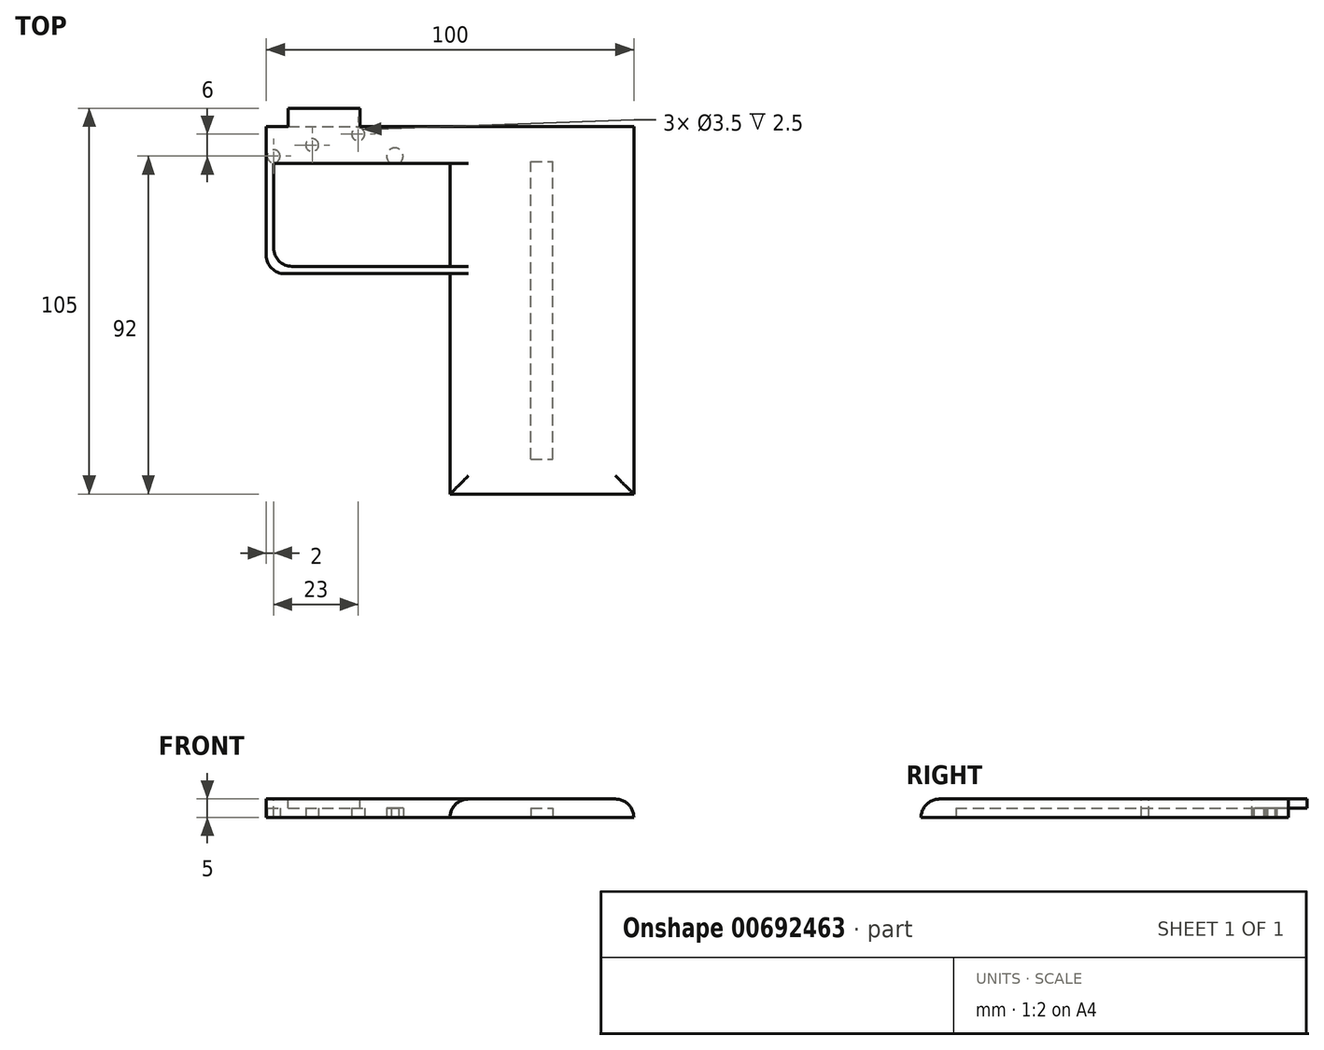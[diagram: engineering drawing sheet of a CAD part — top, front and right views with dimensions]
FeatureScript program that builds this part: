
annotation { "Feature Type Name" : "Feature", "Feature Type Description" : "" }
export const myFeature = defineFeature(function(context is Context, id is Id, definition is map)
    precondition{}
    {
        {
            var Q0;
            Q0=qCreatedBy(makeId("Top.planeOp"),FACE);
            var sketch = newSketch(context, id + "F0", { "sketchPlane" : qUnion([Q0])});
            skLineSegment(sketch, "E0.bottom", {"start": v(25, 50) * mm, "end": v(-25, 50) * mm});
            skLineSegment(sketch, "E0.top", {"start": v(25, -50) * mm, "end": v(-25, -50) * mm});
            skLineSegment(sketch, "E0.left", {"start": v(25, 50) * mm, "end": v(25, -50) * mm});
            skLineSegment(sketch, "E0.right", {"start": v(-25, 50) * mm, "end": v(-25, -50) * mm});
            skPoint(sketch, "E0.middle", {"position": v(0, 0) * mm});
            skLineSegment(sketch, "E1.bottom", {"start": v(-25, 50) * mm, "end": v(-75, 50) * mm});
            skLineSegment(sketch, "E1.top", {"start": v(-25, 10) * mm, "end": v(-75, 10) * mm});
            skLineSegment(sketch, "E1.left", {"start": v(-25, 50) * mm, "end": v(-25, 10) * mm});
            skLineSegment(sketch, "E1.right", {"start": v(-75, 50) * mm, "end": v(-75, 10) * mm});
            skLineSegment(sketch, "E2", {"start": v(-75, 50) * mm, "end": v(-73, 50) * mm});
            skLineSegment(sketch, "E3", {"start": v(-73, 50) * mm, "end": v(-73, 40) * mm});
            skLineSegment(sketch, "E4", {"start": v(-25, 10) * mm, "end": v(-25, 12) * mm});
            skLineSegment(sketch, "E5.bottom", {"start": v(-25, 12) * mm, "end": v(-73, 12) * mm});
            skLineSegment(sketch, "E5.top", {"start": v(-25, 40) * mm, "end": v(-73, 40) * mm});
            skLineSegment(sketch, "E5.left", {"start": v(-25, 12) * mm, "end": v(-25, 40) * mm});
            skLineSegment(sketch, "E5.right", {"start": v(-73, 12) * mm, "end": v(-73, 40) * mm});
            skSolve(sketch);
        }
        {
            var Q0;
            {var subQ0=sQuery(id+"F0.wireOp",EDGE,"E2");Q0=makeQuery(id+"F0.imprint","IMPRINT",FACE,{"disambiguationData":[TD([[makeQuery(id+"F0.imprint","IMPRINT",EDGE,{"derivedFrom":subQ0}),-1.0]])]});}
            var Q1;
            {var subQ2=sQuery(id+"F0.wireOp",EDGE,"E1.top");Q1=makeQuery(id+"F0.imprint","IMPRINT",FACE,{"disambiguationData":[TD([[makeQuery(id+"F0.imprint","IMPRINT",EDGE,{"derivedFrom":subQ2}),-1.0]])]});}
            var Q2;
            {var subQ1=sQuery(id+"F0.wireOp",EDGE,"E0.bottom");Q2=makeQuery(id+"F0.imprint","IMPRINT",FACE,{"disambiguationData":[TD([[makeQuery(id+"F0.imprint","IMPRINT",EDGE,{"derivedFrom":subQ1}),1.0]])]});}
            var Q3;
            {var subQ4=sQuery(id+"F0.wireOp",EDGE,"E1.bottom");Q3=makeQuery(id+"F0.imprint","IMPRINT",FACE,{"disambiguationData":[TD([[makeQuery(id+"F0.imprint","IMPRINT",EDGE,{"derivedFrom":subQ4}),1.0]])]});}
            extrude(context, id + "F1", {"entities" : qUnion([Q0, Q1, Q2, Q3]), "oppositeDirection" : true, "depth" : 5 * mm, "offsetDistance" : 25 * mm});
        }
        {
            var Q0;
            Q0=makeQuery(id+"F1.opExtrude","CAP_EDGE",EDGE,{"disambiguationData":[OSD([sQuery(id+"F0.wireOp",EDGE,"E0.right")])],"isStart":true});
            var Q1;
            Q1=makeQuery(id+"F1.opExtrude","CAP_EDGE",EDGE,{"disambiguationData":[OSD([sQuery(id+"F0.wireOp",EDGE,"E0.top")])],"isStart":true});
            var Q2;
            Q2=makeQuery(id+"F1.opExtrude","CAP_EDGE",EDGE,{"disambiguationData":[OSD([sQuery(id+"F0.wireOp",EDGE,"E0.left")])],"isStart":true});
            var Q3;
            Q3=makeQuery(id+"F1.opExtrude","CAP_EDGE",EDGE,{"disambiguationData":[OSD([sQuery(id+"F0.wireOp",EDGE,"E5.left")])],"isStart":true});
            fillet(context, id + "F2", {"entities" : qUnion([Q0, Q1, Q2, Q3]), "radius" : 5 * mm, "tangentPropagation" : true, "allowEdgeOverflow" : false});
        }
        {
            var Q0;
            Q0=makeQuery(id+"F1.opExtrude","SWEPT_EDGE",EDGE,{"disambiguationData":[OSD([sQuery(id+"F0.wireOp",EDGE,"E5.bottom"),sQuery(id+"F0.wireOp",EDGE,"E5.right")])]});
            var Q1;
            Q1=makeQuery(id+"F1.opExtrude","SWEPT_EDGE",EDGE,{"disambiguationData":[OSD([sQuery(id+"F0.wireOp",EDGE,"E1.top"),sQuery(id+"F0.wireOp",EDGE,"E1.right")])]});
            fillet(context, id + "F3", {"entities" : qUnion([Q0, Q1]), "radius" : 5 * mm, "tangentPropagation" : true, "allowEdgeOverflow" : false});
        }
        {
            var Q0;
            Q0=makeQuery(id+"F1.opExtrude","CAP_FACE",FACE,{"disambiguationData":[OSD([sQuery(id+"F0.wireOp",EDGE,"E0.bottom"),sQuery(id+"F0.wireOp",EDGE,"E0.top"),sQuery(id+"F0.wireOp",EDGE,"E0.left"),sQuery(id+"F0.wireOp",EDGE,"E0.right"),sQuery(id+"F0.wireOp",EDGE,"E1.bottom"),sQuery(id+"F0.wireOp",EDGE,"E1.top"),sQuery(id+"F0.wireOp",EDGE,"E1.right"),sQuery(id+"F0.wireOp",EDGE,"E2"),sQuery(id+"F0.wireOp",EDGE,"E5.bottom"),sQuery(id+"F0.wireOp",EDGE,"E5.top"),sQuery(id+"F0.wireOp",EDGE,"E5.left"),sQuery(id+"F0.wireOp",EDGE,"E5.right")])],"isStart":false});
            var sketch = newSketch(context, id + "F4", { "sketchPlane" : qUnion([Q0])});
            skLineSegment(sketch, "E6", {"start": v(-25, -40) * mm, "end": v(-40, -40) * mm, "construction": true});
            skLineSegment(sketch, "E7", {"start": v(-40, -40) * mm, "end": v(-40, -42) * mm, "construction": true});
            skCircle(sketch, "E8", {"center": v(-40, -42) * mm, "radius": 2.25 * mm});
            skLineSegment(sketch, "E9", {"start": v(-40, -40) * mm, "end": v(-62.5, -40) * mm, "construction": true});
            skLineSegment(sketch, "E10", {"start": v(-62.5, -40) * mm, "end": v(-62.5, -45) * mm, "construction": true});
            skCircle(sketch, "E11", {"center": v(-62.5, -45) * mm, "radius": 1.75 * mm});
            skLineSegment(sketch, "E12", {"start": v(-40, -42) * mm, "end": v(-40, -50) * mm, "construction": true});
            skLineSegment(sketch, "E13", {"start": v(-40, -50) * mm, "end": v(-50, -50) * mm, "construction": true});
            skLineSegment(sketch, "E14", {"start": v(-50, -50) * mm, "end": v(-50, -48) * mm, "construction": true});
            skCircle(sketch, "E15", {"center": v(-50, -48) * mm, "radius": 1.75 * mm});
            skLineSegment(sketch, "E16", {"start": v(-73, -40) * mm, "end": v(-73, -42) * mm});
            skCircle(sketch, "E17", {"center": v(-73, -42) * mm, "radius": 1.75 * mm});
            skLineSegment(sketch, "E18.bottom", {"start": v(-3, 40.5) * mm, "end": v(3, 40.5) * mm});
            skLineSegment(sketch, "E18.top", {"start": v(-3, -40.5) * mm, "end": v(3, -40.5) * mm});
            skLineSegment(sketch, "E18.left", {"start": v(-3, 40.5) * mm, "end": v(-3, -40.5) * mm});
            skLineSegment(sketch, "E18.right", {"start": v(3, 40.5) * mm, "end": v(3, -40.5) * mm});
            skPoint(sketch, "E18.middle", {"position": v(0, 0) * mm});
            skSolve(sketch);
        }
        {
            var Q0;
            Q0=makeQuery(id+"F4.imprint","IMPRINT",FACE,{"disambiguationData":[TD([[makeQuery(id+"F4.imprint","IMPRINT",EDGE,{"derivedFrom":sQuery(id+"F4.wireOp",EDGE,"E18.bottom")}),-1.0]])]});
            var Q1;
            {var subQ0=sQuery(id+"F4.wireOp",EDGE,"E8");var subQ1=makeQuery(id+"F1.opExtrude","CAP_EDGE",EDGE,{"disambiguationData":[OSD([sQuery(id+"F0.wireOp",EDGE,"E5.top")])],"isStart":false});var subQ2=makeQuery(id+"F4.imprint","INTERSECT",VERTEX,{"disambiguationData":[OD(0.0)],"derivedFrom":[subQ1,subQ0]});Q1=makeQuery(id+"F4.imprint","IMPRINT",FACE,{"disambiguationData":[TD([[makeQuery(id+"F4.imprint","IMPRINT",EDGE,{"disambiguationData":[TD([[subQ2,-1.0]])],"derivedFrom":subQ0}),1.0]])]});}
            var Q2;
            Q2=makeQuery(id+"F4.imprint","IMPRINT",FACE,{"disambiguationData":[TD([[makeQuery(id+"F4.imprint","IMPRINT",EDGE,{"derivedFrom":sQuery(id+"F4.wireOp",EDGE,"E15")}),1.0]])]});
            var Q3;
            Q3=makeQuery(id+"F4.imprint","IMPRINT",FACE,{"disambiguationData":[TD([[makeQuery(id+"F4.imprint","IMPRINT",EDGE,{"derivedFrom":sQuery(id+"F4.wireOp",EDGE,"E11")}),1.0]])]});
            var Q4;
            Q4=makeQuery(id+"F4.imprint","IMPRINT",FACE,{"disambiguationData":[TD([[makeQuery(id+"F4.imprint","IMPRINT",EDGE,{"derivedFrom":sQuery(id+"F4.wireOp",EDGE,"E17")}),1.0]])]});
            extrude(context, id + "F5", {"entities" : qUnion([Q0, Q1, Q2, Q3, Q4]), "operationType" : NewBodyOperationType.REMOVE, "oppositeDirection" : true, "depth" : 2.5 * mm, "offsetDistance" : 25 * mm});
        }
        {
            var Q0;
            Q0=makeQuery(id+"F1.opExtrude","SWEPT_FACE",FACE,{"disambiguationData":[OSD([sQuery(id+"F0.wireOp",EDGE,"E0.bottom"),sQuery(id+"F0.wireOp",EDGE,"E1.bottom"),sQuery(id+"F0.wireOp",EDGE,"E2")])]});
            var sketch = newSketch(context, id + "F6", { "sketchPlane" : qUnion([Q0])});
            skLineSegment(sketch, "E19", {"start": v(75, 0) * mm, "end": v(75, -2.5) * mm});
            skLineSegment(sketch, "E20", {"start": v(75, -2.5) * mm, "end": v(69, -2.5) * mm});
            skLineSegment(sketch, "E21", {"start": v(69, -2.5) * mm, "end": v(49.5, -2.5) * mm});
            skLineSegment(sketch, "E22", {"start": v(49.5, -2.5) * mm, "end": v(49.5, 0) * mm});
            skLineSegment(sketch, "E23", {"start": v(69, -2.5) * mm, "end": v(69, 0) * mm});
            skSolve(sketch);
        }
        {
            var Q0;
            Q0=makeQuery(id+"F6.imprint","IMPRINT",FACE,{"disambiguationData":[TD([[makeQuery(id+"F6.imprint","IMPRINT",EDGE,{"derivedFrom":sQuery(id+"F6.wireOp",EDGE,"E21")}),-1.0]])]});
            extrude(context, id + "F7", {"entities" : qUnion([Q0]), "operationType" : NewBodyOperationType.ADD, "depth" : 5 * mm, "offsetDistance" : 25 * mm});
        }
    });
